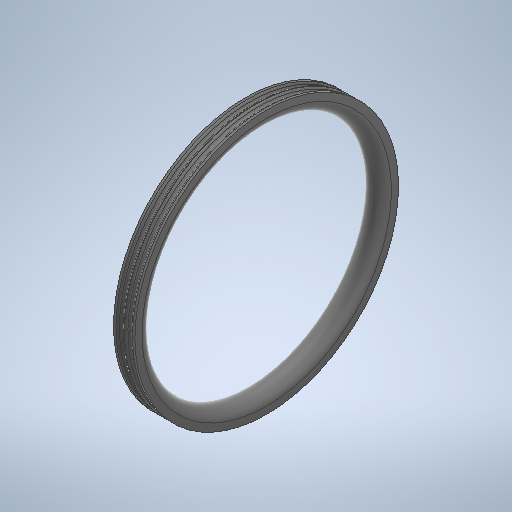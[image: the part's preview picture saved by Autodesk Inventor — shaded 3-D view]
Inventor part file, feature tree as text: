
AUTODESK INVENTOR PART (.ipt)
format: ipt  version: 2025.2 (Build 292293000, 293)  size: 368,128 bytes
history: native  units: in
note: dims shown in document units (in); Inventor stores cm internally (conversion verified against a paired STEP export)
features: revolve x1, fillet x1, sketch x1
ambient origin geometry x8: Origin, YZ Plane, XZ Plane, XY Plane, X Axis, Y Axis, Z Axis, Center Point
bodies: Body1 (feature_tree)
feature tree (3):
  revolve  "Revolution2"  [1 undecoded]
  fillet  "Fillet1"  Radius=0.1969in
  sketch  "Sketch3"  dims[d33=360.0deg d34=0.0in d51=0.1969in d52=0.1181in d53=0.0787in d54=0.1181in d55=0.0787in d56=0.0591in]
note: 1 required parameter value undecoded (feature->parameter linkage not recoverable at this tier; creation-order binding heuristic only, values carry confidence <= 0.55)
